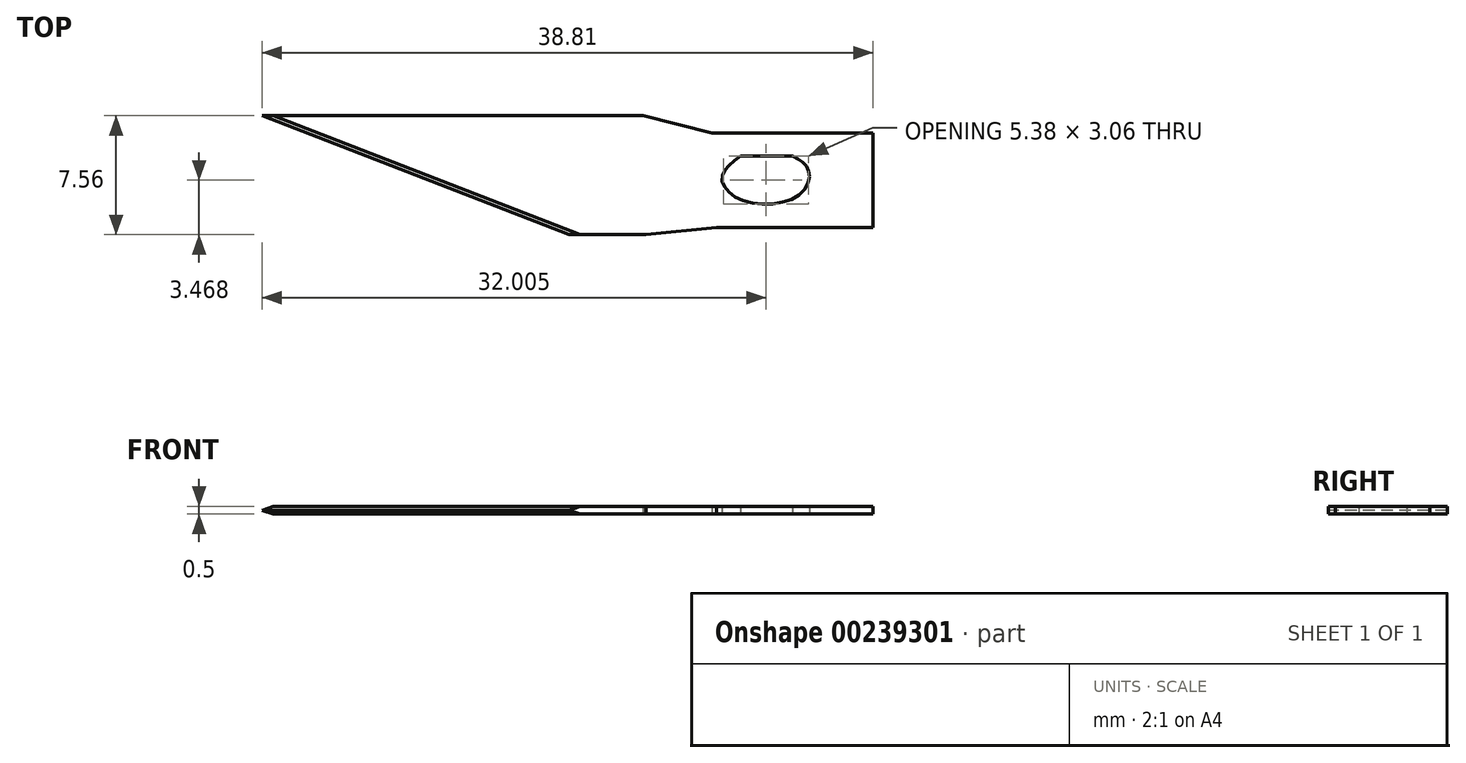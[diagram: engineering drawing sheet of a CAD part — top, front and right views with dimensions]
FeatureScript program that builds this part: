
annotation { "Feature Type Name" : "Feature", "Feature Type Description" : "" }
export const myFeature = defineFeature(function(context is Context, id is Id, definition is map)
    precondition{}
    {
        {
            var Q0;
            Q0=qCreatedBy(makeId("Top.planeOp"),FACE);
            var sketch = newSketch(context, id + "F0", { "sketchPlane" : qUnion([Q0])});
            skLineSegment(sketch, "E0", {"start": v(-12.3, -11.29) * mm, "end": v(12.58, -11.29) * mm});
            skLineSegment(sketch, "E1", {"start": v(12.58, -11.29) * mm, "end": v(16.96, -12.38) * mm});
            skLineSegment(sketch, "E2", {"start": v(16.96, -12.38) * mm, "end": v(27.2, -12.38) * mm});
            skLineSegment(sketch, "E3", {"start": v(27.2, -12.38) * mm, "end": v(27.2, -18.38) * mm});
            skLineSegment(sketch, "E4", {"start": v(27.2, -18.38) * mm, "end": v(17.26, -18.38) * mm});
            skLineSegment(sketch, "E5", {"start": v(17.26, -18.38) * mm, "end": v(12.78, -18.85) * mm});
            skLineSegment(sketch, "E6", {"start": v(12.78, -18.85) * mm, "end": v(7.21, -18.85) * mm});
            skLineSegment(sketch, "E7", {"start": v(7.21, -18.85) * mm, "end": v(-12.3, -11.29) * mm});
            skLineSegment(sketch, "E8", {"start": v(18.78, -13.85) * mm, "end": v(22.09, -13.85) * mm});
            skPoint(sketch, "E8.endSnap0", {"position": v(22.09, -12.38) * mm});
            skFitSpline(sketch, "E9", {"points": [v(22.09, -13.85) * mm, v(23.08, -14.7) * mm, v(22.52, -16.31) * mm, v(18.84, -16.65) * mm, v(17.61, -15.2) * mm, v(18.78, -13.85) * mm], "startDerivative": vector(7.83, -4.05) * mm, "endDerivative": vector(8.91, 6.67) * mm});
            skSolve(sketch);
        }
        {
            var Q0;
            Q0 = qSketchRegion(id + "F0", true);
            extrude(context, id + "F1", {"entities" : qUnion([Q0]), "depth" : .5 * mm});
        }
        {
            var Q0;
            Q0=makeQuery(id+"F1.opExtrude","CAP_EDGE",EDGE,{"disambiguationData":[OSD([sQuery(id+"F0.wireOp",EDGE,"E7")])],"isStart":false});
            var Q1;
            Q1=makeQuery(id+"F1.opExtrude","CAP_EDGE",EDGE,{"disambiguationData":[OSD([sQuery(id+"F0.wireOp",EDGE,"E7")])],"isStart":true});
            chamfer(context, id + "F2", {"entities" : qUnion([Q0, Q1]), "width" : .5 * mm, "tangentPropagation" : true});
        }
    });
